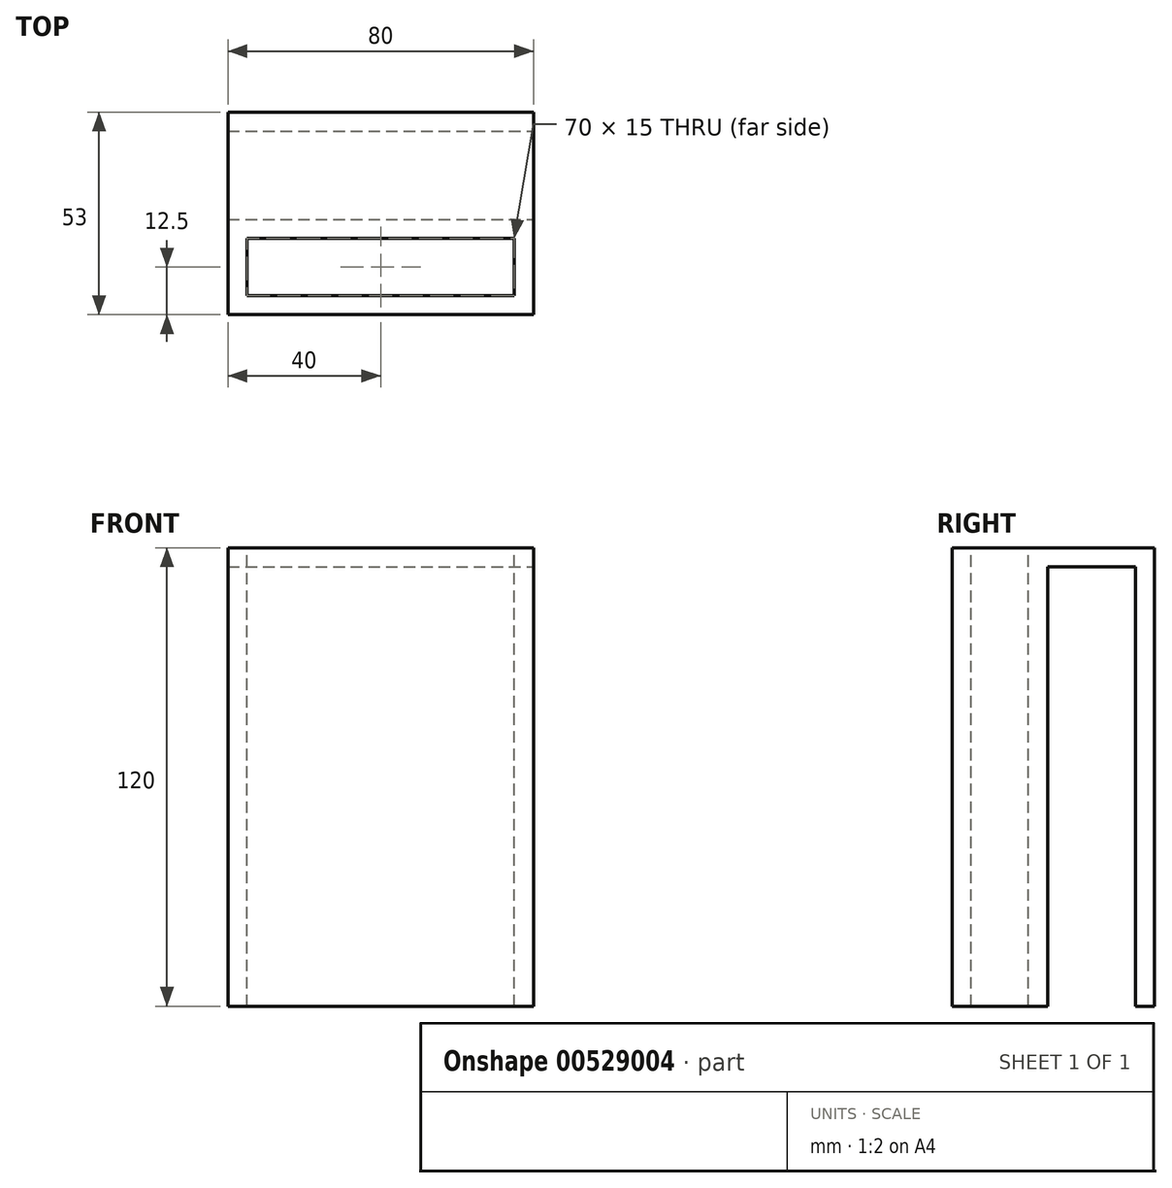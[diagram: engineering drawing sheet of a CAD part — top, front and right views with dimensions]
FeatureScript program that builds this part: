
annotation { "Feature Type Name" : "Feature", "Feature Type Description" : "" }
export const myFeature = defineFeature(function(context is Context, id is Id, definition is map)
    precondition{}
    {
        {
            var Q0;
            Q0=qCreatedBy(makeId("Right.planeOp"),FACE);
            var sketch = newSketch(context, id + "F0", { "sketchPlane" : qUnion([Q0])});
            skLineSegment(sketch, "E0", {"start": v(0, -44.86) * mm, "end": v(0, 75.14) * mm});
            skLineSegment(sketch, "E1", {"start": v(-5, 70.14) * mm, "end": v(-5, -44.86) * mm});
            skLineSegment(sketch, "E2", {"start": v(-5, 70.14) * mm, "end": v(-28, 70.14) * mm});
            skLineSegment(sketch, "E3", {"start": v(-28, 70.14) * mm, "end": v(-28, -44.86) * mm});
            skLineSegment(sketch, "E4", {"start": v(-28, -44.86) * mm, "end": v(-53, -44.86) * mm});
            skLineSegment(sketch, "E5", {"start": v(-53, -44.86) * mm, "end": v(-53, 75.14) * mm});
            skLineSegment(sketch, "E6", {"start": v(-53, 75.14) * mm, "end": v(0, 75.14) * mm});
            skLineSegment(sketch, "E7", {"start": v(-5, -44.86) * mm, "end": v(0, -44.86) * mm});
            skSolve(sketch);
        }
        {
            var Q0;
            Q0 = qSketchRegion(id + "F0", true);
            extrude(context, id + "F1", {"entities" : qUnion([Q0]), "oppositeDirection" : true, "depth" : 80 * mm, "offsetDistance" : 25 * mm});
        }
        {
            var Q0;
            Q0=makeQuery(id+"F1.opExtrude","SWEPT_FACE",FACE,{"disambiguationData":[OSD([sQuery(id+"F0.wireOp",EDGE,"E6")])]});
            var sketch = newSketch(context, id + "F2", { "sketchPlane" : qUnion([Q0])});
            skLineSegment(sketch, "E8.0", {"start": v(-80, -28) * mm, "end": v(0, -28) * mm});
            skLineSegment(sketch, "E9", {"start": v(-80, -28) * mm, "end": v(-80, -53) * mm});
            skLineSegment(sketch, "E10", {"start": v(-80, -53) * mm, "end": v(0, -53) * mm});
            skLineSegment(sketch, "E11", {"start": v(0, -53) * mm, "end": v(0, -28) * mm});
            skLineSegment(sketch, "E12.0", {"start": v(-75, -33) * mm, "end": v(-75, -48) * mm});
            skLineSegment(sketch, "E12.1", {"start": v(-75, -33) * mm, "end": v(-5, -33) * mm});
            skLineSegment(sketch, "E12.2", {"start": v(-5, -48) * mm, "end": v(-5, -33) * mm});
            skLineSegment(sketch, "E12.3", {"start": v(-75, -48) * mm, "end": v(-5, -48) * mm});
            skSolve(sketch);
        }
        {
            var Q0;
            Q0=makeQuery(id+"F2.imprint","IMPRINT",FACE,{"disambiguationData":[TD([[makeQuery(id+"F2.imprint","IMPRINT",EDGE,{"derivedFrom":sQuery(id+"F2.wireOp",EDGE,"E12.0")}),1.0]])]});
            extrude(context, id + "F3", {"entities" : qUnion([Q0]), "operationType" : NewBodyOperationType.REMOVE, "endBound" : BoundingType.THROUGH_ALL, "oppositeDirection" : true, "depth" : 25 * mm, "offsetDistance" : 25 * mm});
        }
    });
